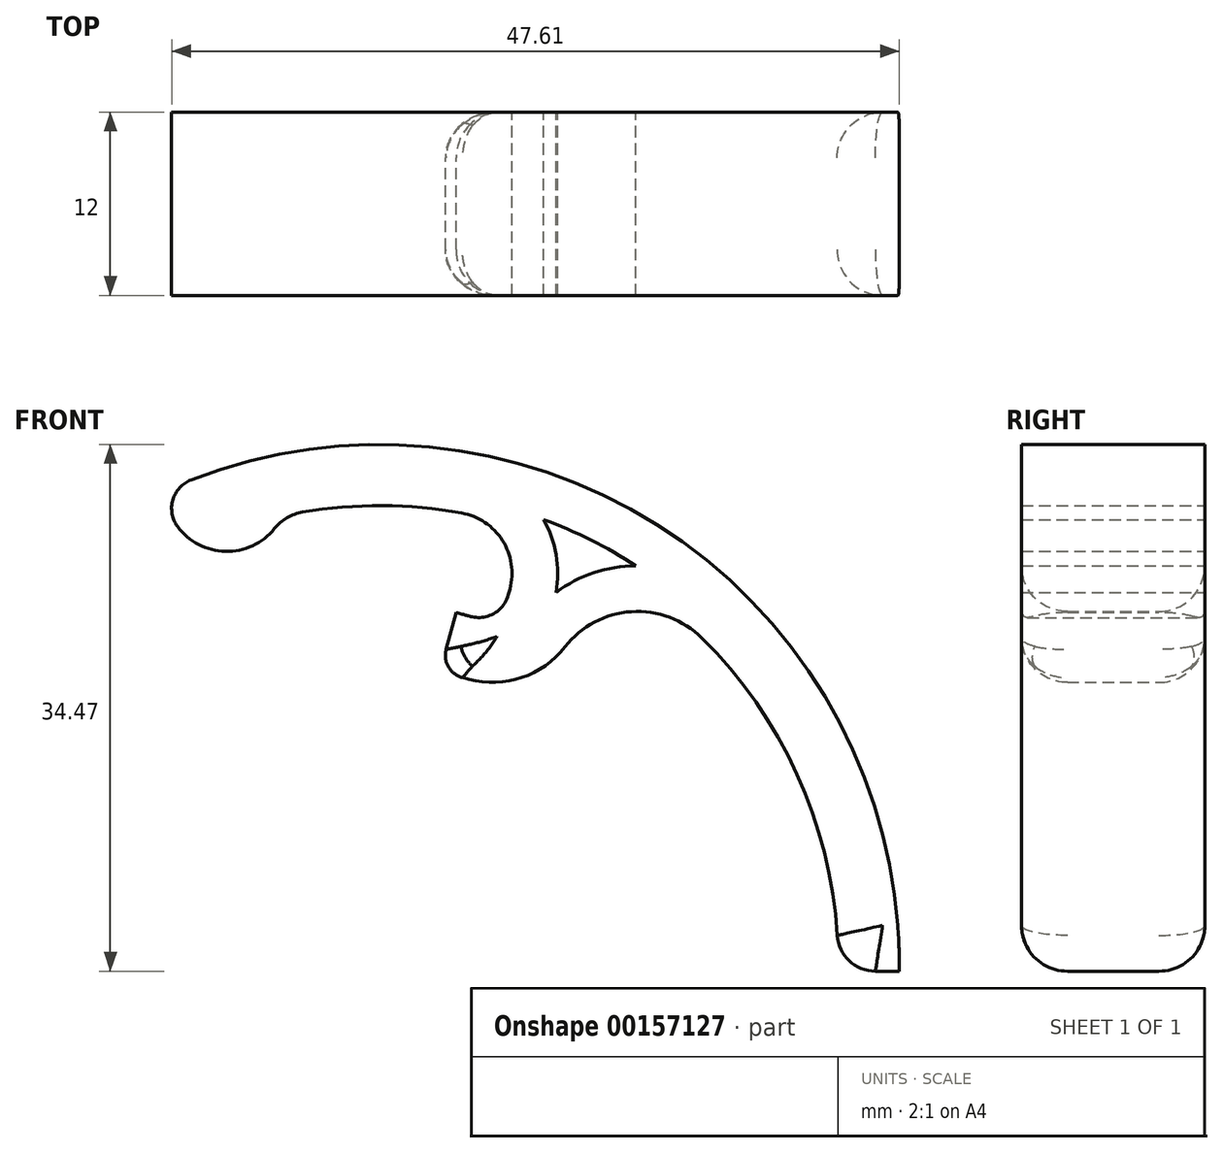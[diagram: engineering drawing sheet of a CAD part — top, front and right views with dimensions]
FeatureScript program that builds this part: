
annotation { "Feature Type Name" : "Feature", "Feature Type Description" : "" }
export const myFeature = defineFeature(function(context is Context, id is Id, definition is map)
    precondition{}
    {
        {
            var Q0;
            Q0=qCreatedBy(makeId("Front.planeOp"),FACE);
            var sketch = newSketch(context, id + "F0", { "sketchPlane" : qUnion([Q0])});
            skLineSegment(sketch, "E0", {"start": v(0, 0) * mm, "end": v(0.97, -0.26) * mm});
            skLineSegment(sketch, "E1", {"start": v(3.42, 1.16) * mm, "end": v(3.52, 1.54) * mm});
            skArc(sketch, "E2", {"start": v(24.94, -21.12) * mm, "mid": v(22.3, -10.58) * mm, "end": v(16.09, -1.66) * mm});
            skArc(sketch, "E3", {"start": v(-18.23, 5.64) * mm, "mid": v(-15.09, 4) * mm, "end": v(-11.88, 5.5) * mm});
            skArc(sketch, "E4.0", {"start": v(29, -23.47) * mm, "mid": v(14.38, 4.93) * mm, "end": v(-17.34, 8.68) * mm});
            skLineSegment(sketch, "E4.1", {"start": v(5.73, -5.68) * mm, "end": v(5.86, -5.19) * mm});
            skLineSegment(sketch, "E4.2", {"start": v(0.41, -4.25) * mm, "end": v(0.84, -4.37) * mm});
            skLineSegment(sketch, "E5", {"start": v(-0.65, -2.41) * mm, "end": v(0, 0) * mm});
            skArc(sketch, "E6.trimOffspring", {"start": v(0.37, 6.52) * mm, "mid": v(-4.84, 7) * mm, "end": v(-10.05, 6.57) * mm});
            skLineSegment(sketch, "E7", {"start": v(27.44, -23.47) * mm, "end": v(29.4, -23.47) * mm});
            skPoint(sketch, "E8.visualSharp", {"position": v(4.56, 5.44) * mm});
            skArc(sketch, "E8.filletArc", {"start": v(3.52, 1.54) * mm, "mid": v(3.04, 4.72) * mm, "end": v(0.37, 6.52) * mm});
            skPoint(sketch, "E9.visualSharp", {"position": v(2.9, -0.78) * mm});
            skArc(sketch, "E9.filletArc", {"start": v(0.97, -0.26) * mm, "mid": v(2.48, -0.06) * mm, "end": v(3.42, 1.16) * mm});
            skPoint(sketch, "E10.visualSharp", {"position": v(8.3, 3.9) * mm});
            skArc(sketch, "E10.filletArc", {"start": v(16.09, -1.66) * mm, "mid": v(11.48, 0.06) * mm, "end": v(7.13, -2.25) * mm});
            skArc(sketch, "E11.filletArc", {"start": v(0.84, -4.37) * mm, "mid": v(4.3, -4.26) * mm, "end": v(7.13, -2.25) * mm});
            skPoint(sketch, "E12.visualSharp", {"position": v(-1.04, -3.86) * mm});
            skArc(sketch, "E12.filletArc", {"start": v(-0.65, -2.41) * mm, "mid": v(-0.5, -3.55) * mm, "end": v(0.41, -4.25) * mm});
            skPoint(sketch, "E13.visualSharp", {"position": v(-19, 7.98) * mm});
            skArc(sketch, "E13.filletArc", {"start": v(-17.34, 8.68) * mm, "mid": v(-18.53, 7.38) * mm, "end": v(-18.23, 5.64) * mm});
            skArc(sketch, "E14.filletArc", {"start": v(24.94, -21.12) * mm, "mid": v(25.72, -22.8) * mm, "end": v(27.44, -23.47) * mm});
            skPoint(sketch, "E15.visualSharp", {"position": v(-11.37, 6.32) * mm});
            skArc(sketch, "E15.filletArc", {"start": v(-10.05, 6.57) * mm, "mid": v(-11.06, 6.2) * mm, "end": v(-11.88, 5.5) * mm});
            skArc(sketch, "E16.0", {"start": v(18.2, 0.47) * mm, "mid": v(11.28, 3.05) * mm, "end": v(4.76, -0.4) * mm});
            skArc(sketch, "E17.0", {"start": v(6.42, 0.77) * mm, "mid": v(5.57, 6.32) * mm, "end": v(0.9, 9.47) * mm});
            skArc(sketch, "E18.0", {"start": v(26, -22.97) * mm, "mid": v(12.48, 2.6) * mm, "end": v(-16.25, 5.89) * mm});
            skSolve(sketch);
        }
        {
            var Q0;
            Q0 = qSketchRegion(id + "F0", true);
            extrude(context, id + "F1", {"entities" : qUnion([Q0]), "depth" : 12 * mm});
        }
        {
            var Q0;
            Q0=makeQuery(id+"F1.opExtrude","CAP_EDGE",EDGE,{"disambiguationData":[OSD([sQuery(id+"F0.wireOp",EDGE,"E7")])],"isStart":false});
            var Q1;
            Q1=makeQuery(id+"F1.opExtrude","CAP_EDGE",EDGE,{"disambiguationData":[OSD([sQuery(id+"F0.wireOp",EDGE,"E7")])],"isStart":true});
            fillet(context, id + "F2", {"entities" : qUnion([Q0, Q1]), "radius" : 3 * mm, "tangentPropagation" : true, "allowEdgeOverflow" : false});
        }
    });
